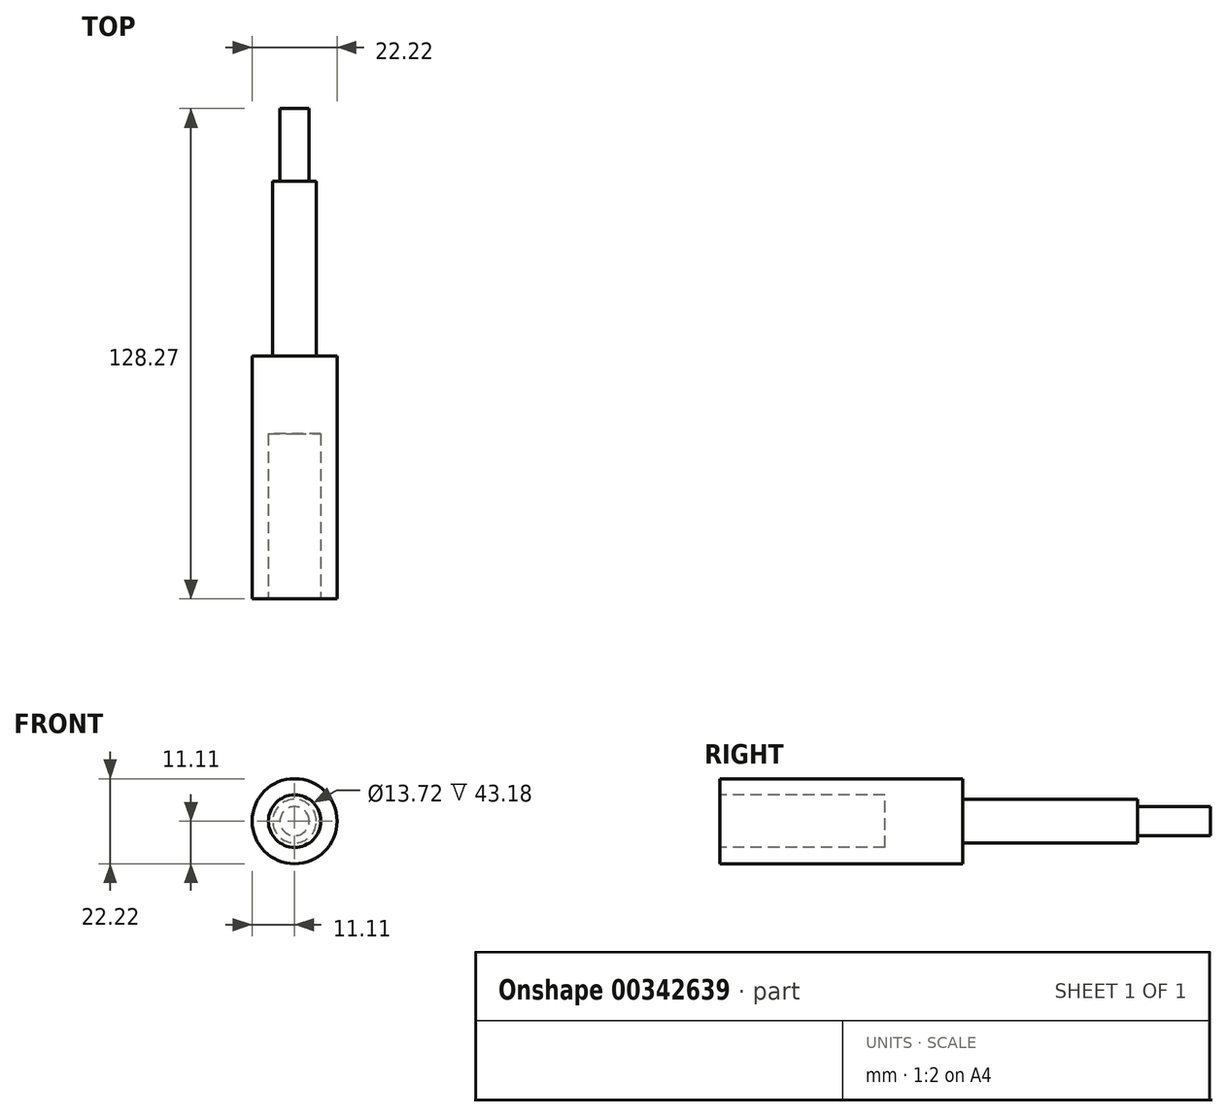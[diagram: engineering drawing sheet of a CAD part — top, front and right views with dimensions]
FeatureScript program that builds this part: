
annotation { "Feature Type Name" : "Feature", "Feature Type Description" : "" }
export const myFeature = defineFeature(function(context is Context, id is Id, definition is map)
    precondition{}
    {
        {
            var Q0;
            Q0=qCreatedBy(makeId("Front.planeOp"),FACE);
            var sketch = newSketch(context, id + "F0", { "sketchPlane" : qUnion([Q0])});
            skCircle(sketch, "E0", {"center": v(0, 0) * mm, "radius": 5.72 * mm});
            skSolve(sketch);
        }
        {
            var Q0;
            Q0 = qSketchRegion(id + "F0", true);
            extrude(context, id + "F1", {"entities" : qUnion([Q0]), "depth" : 45.72 * mm});
        }
        {
            var Q0;
            Q0=makeQuery(id+"F1.opExtrude","CAP_FACE",FACE,{"disambiguationData":[OSD([sQuery(id+"F0.wireOp",EDGE,"E0")])],"isStart":false});
            cPlane(context, id + "F2", {"entities" : qUnion([Q0]), "cplaneType" : CPlaneType.OFFSET, "offset" : 0 * mm, "width" : 152.4 * mm, "height" : 152.4 * mm});
        }
        {
            var Q0;
            Q0=qCreatedBy(id+"F2.planeOp",FACE);
            var sketch = newSketch(context, id + "F3", { "sketchPlane" : qUnion([Q0])});
            skCircle(sketch, "E1", {"center": v(0, 0) * mm, "radius": 11.11 * mm});
            skSolve(sketch);
        }
        {
            var Q0;
            Q0 = qSketchRegion(id + "F3", true);
            extrude(context, id + "F4", {"entities" : qUnion([Q0]), "operationType" : NewBodyOperationType.ADD, "depth" : 63.5 * mm});
        }
        {
            var Q0;
            Q0=makeQuery(id+"F4.opExtrude","CAP_FACE",FACE,{"disambiguationData":[OSD([sQuery(id+"F3.wireOp",EDGE,"E1")])],"isStart":false});
            cPlane(context, id + "F5", {"entities" : qUnion([Q0]), "cplaneType" : CPlaneType.OFFSET, "offset" : 0 * mm, "width" : 152.4 * mm, "height" : 152.4 * mm});
        }
        {
            var Q0;
            Q0=qCreatedBy(id+"F5.planeOp",FACE);
            var sketch = newSketch(context, id + "F6", { "sketchPlane" : qUnion([Q0])});
            skCircle(sketch, "E2", {"center": v(0, 0) * mm, "radius": 6.86 * mm});
            skSolve(sketch);
        }
        {
            var Q0;
            Q0 = qSketchRegion(id + "F6", true);
            extrude(context, id + "F7", {"entities" : qUnion([Q0]), "operationType" : NewBodyOperationType.REMOVE, "oppositeDirection" : true, "depth" : 43.18 * mm});
        }
        {
            var Q0;
            Q0=makeQuery(id+"F1.opExtrude","CAP_FACE",FACE,{"disambiguationData":[OSD([sQuery(id+"F0.wireOp",EDGE,"E0")])],"isStart":true});
            cPlane(context, id + "F8", {"entities" : qUnion([Q0]), "cplaneType" : CPlaneType.OFFSET, "offset" : 0 * mm, "width" : 152.4 * mm, "height" : 152.4 * mm});
        }
        {
            var Q0;
            Q0=qCreatedBy(id+"F8.planeOp",FACE);
            var sketch = newSketch(context, id + "F9", { "sketchPlane" : qUnion([Q0])});
            skCircle(sketch, "E3", {"center": v(0, 0) * mm, "radius": 3.81 * mm});
            skSolve(sketch);
        }
        {
            var Q0;
            Q0 = qSketchRegion(id + "F9", true);
            extrude(context, id + "F10", {"entities" : qUnion([Q0]), "operationType" : NewBodyOperationType.ADD, "depth" : 19.05 * mm});
        }
    });
